# Revit family: P190780JX-112c_JGC3530GS_StainlessSteel_JA_Cooking_Cooktops
name_source: partatom
category: Specialty Equipment
units: mm (PartAtom-declared; Revit-internal decimal feet)

## family parameters
Always vertical = Yes
Cut with Voids When Loaded = No
Enable Cutting in Views = No
Maintain Annotation Orientation = No
Part Type = Normal
Room Calculation Point = No
Round Connector Dimension = Use Diameter
Shared = No
Work Plane-Based = No

## types (1)
- JGC3530GS
    Amps = 15 A
    Body Material = ARCAT - Metal - Steel - Stainless
    Cooking Grate Material = ARCAT - Metal - Cast Iron 1/4" Plate
    Default Elevation = 0"
    Depth = 21"
    Description = Euro-Style 30" 5-Burner Gas Cooktop
Table de cuisson au gaz, 30 po, 5 brûleurs
    Dimension Guide = http://access.whirlpool.com Guide&sku=JGC3530GS&language=EN
http://access.whirlpool.com Guide&sku=JGC3530GS&language=EN
    Family Name = GAS UPDRAFT COOKTOP - 30"
    Feature 1 = 20,000 BTU Dual-Stacked PowerBurner
Brûleur superposé Power de 20 000 BTU
    Feature 2 = Single Point Electronic Ignition and Flame-Sensing™ Re-ignition
Allumage électronique en un seul point et rallumage à détection Flame-Sensing™
    Feature 3 = 6,000 BTU Simmer Burner with Melt Cap
Brûleur de mijotage avec chapeau de brûleur, 6000 BTU
    Height = 4 1/2"
    Installation-Fabrication = http://access.whirlpool.com Instruction&sku=JGC3530GS&language=EN
http://access.whirlpool.com Instruction&sku=JGC3530GS&language=FR
    Knob Material = ARCAT - Metal - Steel - Stainless
    Manufacturer = Jenn Air
    Model = JGC3530GS
    Voltage = 0 V
    Width = 30"

## geometry (parser evidence)
native form markers: Sweep x3
no freeform markers — native parametric forms only
